# Revit family: Haworth_Torei_Table_Round
name_source: partatom
category: Furniture
revit_build: Autodesk Revit 2018 (Build: 20170223_1515(x64)
units: mm (PartAtom-declared; Revit-internal decimal feet)

## family parameters
Always vertical = Yes
Cut with Voids When Loaded = No
OmniClass Number = 23.40.20.00
OmniClass Title = General Furniture and Specialties
Room Calculation Point = No
Shared = No
Work Plane-Based = No

## types (1)
- HCCS-2015
    Actual Diameter = 15.3 "
    Actual Height = 20 "
    Assembly Code = E2020200
    Base Finish = Haworth _ Paint _ Collection Black
    Description = Haworth Torei Table Round - 15w 20h
    Manufacturer = Haworth
    Model = HCCS-2015
    Standard Diameter = 15.3 Inches
    Standard Height = 20 Inches
    URL = http://www.haworth.com
    URL - Product = https://www.haworth.com
    Version = 3
    Warranty = http://www.haworth.com

## geometry (parser evidence)
native form markers: Blend x6, Sweep x2
no freeform markers — native parametric forms only
